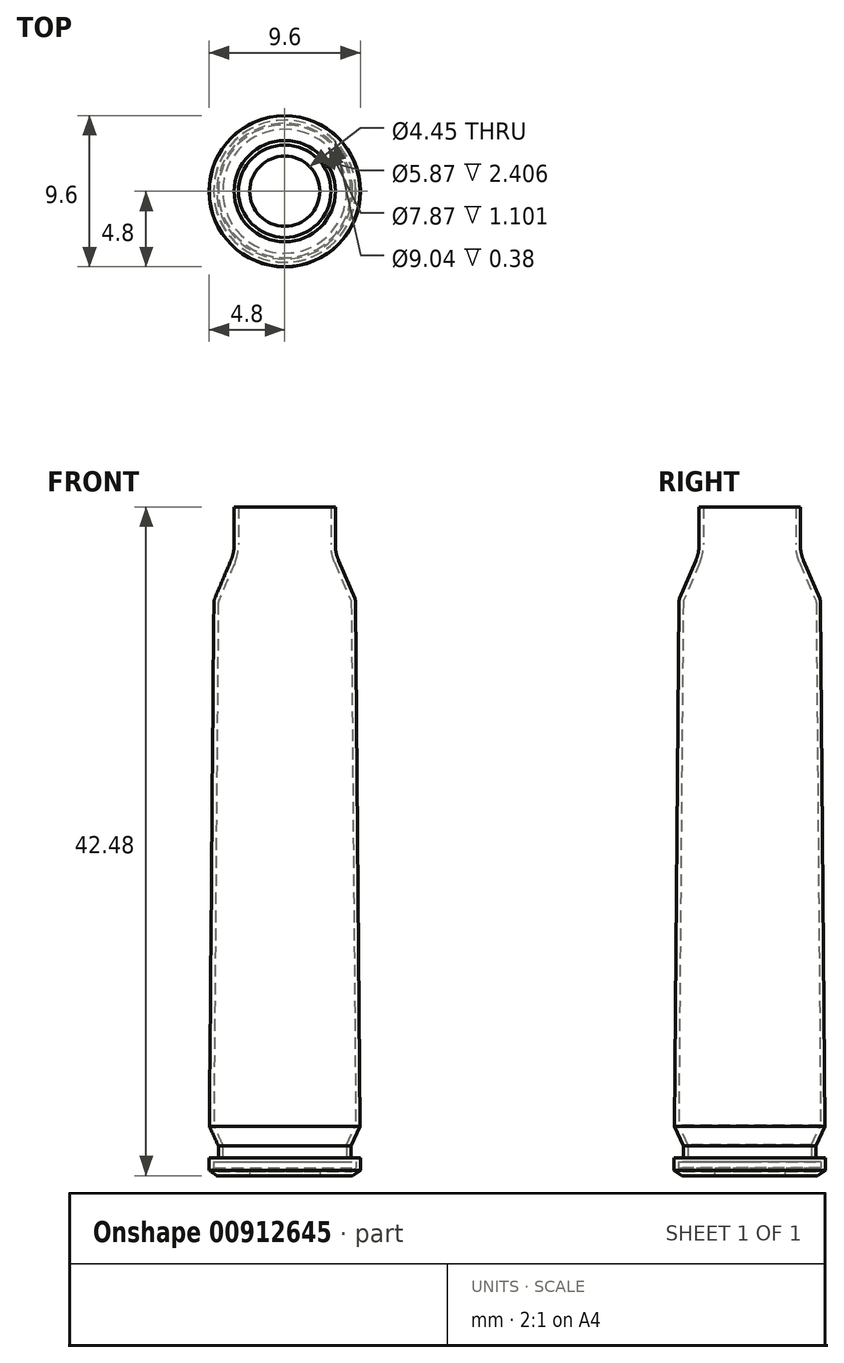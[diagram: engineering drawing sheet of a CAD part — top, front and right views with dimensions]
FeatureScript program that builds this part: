
annotation { "Feature Type Name" : "Feature", "Feature Type Description" : "" }
export const myFeature = defineFeature(function(context is Context, id is Id, definition is map)
    precondition{}
    {
        {
            var Q0;
            Q0=qCreatedBy(makeId("Front.planeOp"),FACE);
            var sketch = newSketch(context, id + "F0", { "sketchPlane" : qUnion([Q0])});
            skLineSegment(sketch, "E0", {"start": v(4.31, -41.16) * mm, "end": v(4.8, -40.82) * mm});
            skLineSegment(sketch, "E1", {"start": v(4.8, -40.82) * mm, "end": v(4.8, -40.01) * mm});
            skLineSegment(sketch, "E2", {"start": v(4.8, -40.01) * mm, "end": v(4.22, -40.01) * mm});
            skLineSegment(sketch, "E3", {"start": v(4.22, -40.01) * mm, "end": v(4.22, -39.25) * mm});
            skLineSegment(sketch, "E4", {"start": v(4.22, -39.25) * mm, "end": v(4.79, -38.02) * mm});
            skLineSegment(sketch, "E5", {"start": v(4.79, -38.02) * mm, "end": v(4.5, -4.76) * mm});
            skPoint(sketch, "E6", {"position": v(0, 5.97) * mm});
            skLineSegment(sketch, "E7", {"start": v(4.45, -4.52) * mm, "end": v(3.42, -2.08) * mm});
            skLineSegment(sketch, "E8", {"start": v(3.22, 1.32) * mm, "end": v(3.22, -1.09) * mm});
            skPoint(sketch, "E9.visualSharp", {"position": v(4.5, -4.63) * mm});
            skArc(sketch, "E9.filletArc", {"start": v(4.5, -4.76) * mm, "mid": v(4.49, -4.64) * mm, "end": v(4.45, -4.52) * mm});
            skPoint(sketch, "E10.visualSharp", {"position": v(3.22, -1.6) * mm});
            skArc(sketch, "E10.filletArc", {"start": v(3.22, -1.09) * mm, "mid": v(3.27, -1.6) * mm, "end": v(3.42, -2.08) * mm});
            skLineSegment(sketch, "E11", {"start": v(0, -41.15) * mm, "end": v(0, 1.32) * mm});
            skLineSegment(sketch, "E12", {"start": v(4.31, -41.16) * mm, "end": v(2.23, -41.16) * mm});
            skLineSegment(sketch, "E13.2", {"start": v(4.52, -40.3) * mm, "end": v(3.94, -40.3) * mm});
            skLineSegment(sketch, "E13.3", {"start": v(4.52, -40.67) * mm, "end": v(4.52, -40.3) * mm});
            skLineSegment(sketch, "E13.4", {"start": v(4.23, -40.88) * mm, "end": v(4.52, -40.67) * mm});
            skLineSegment(sketch, "E13.5", {"start": v(4.23, -40.88) * mm, "end": v(2.23, -40.88) * mm});
            skLineSegment(sketch, "E13.6", {"start": v(3.94, -40.3) * mm, "end": v(3.94, -39.2) * mm});
            skLineSegment(sketch, "E13.7", {"start": v(3.94, -39.2) * mm, "end": v(4.5, -37.96) * mm});
            skLineSegment(sketch, "E13.8", {"start": v(4.5, -37.96) * mm, "end": v(4.22, -4.76) * mm});
            skArc(sketch, "E13.9", {"start": v(4.22, -4.76) * mm, "mid": v(4.22, -4.7) * mm, "end": v(4.2, -4.63) * mm});
            skLineSegment(sketch, "E13.10", {"start": v(4.2, -4.63) * mm, "end": v(3.16, -2.19) * mm});
            skArc(sketch, "E13.11", {"start": v(2.94, -1.09) * mm, "mid": v(3, -1.65) * mm, "end": v(3.16, -2.19) * mm});
            skLineSegment(sketch, "E14", {"start": v(2.23, -41.16) * mm, "end": v(2.23, -40.88) * mm});
            skLineSegment(sketch, "E15", {"start": v(2.94, -1.09) * mm, "end": v(2.94, 1.32) * mm});
            skLineSegment(sketch, "E16", {"start": v(2.94, 1.32) * mm, "end": v(3.22, 1.32) * mm});
            skSolve(sketch);
        }
        {
            var Q0;
            Q0=qSketchRegion(id+"F0",true);
            var Q1;
            Q1=sQuery(id+"F0.wireOp",EDGE,"E11");
            revolve(context, id + "F1", {"surfaceOperationType" : NewSurfaceOperationType.NEW, "entities" : qUnion([Q0]), "axis" : qUnion([Q1]), "revolveType" : RevolveType.FULL});
        }
    });
